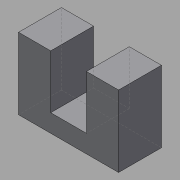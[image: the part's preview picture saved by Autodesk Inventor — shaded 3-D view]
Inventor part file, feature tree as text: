
AUTODESK INVENTOR PART (.ipt)
format: ipt  version: 2015 (Build 190159000, 159)  size: 77,312 bytes
history: native  units: in
note: dims shown in document units (in); Inventor stores cm internally (conversion verified against a paired STEP export)
features: other x3, sketch x2
ambient origin geometry x8: Origin, YZ Plane, XZ Plane, XY Plane, X Axis, Y Axis, Z Axis, Center Point
bodies: Solid1 (feature_tree)
feature tree (5):
  other  "opto_MIR4.ipt"
  other  "Solid1::opto_MIR4.ipt"
  other  "TaggingFeature1"
  sketch  "Sketch1"  dims[d0=0.3937in]
  sketch  "Sketch2"
